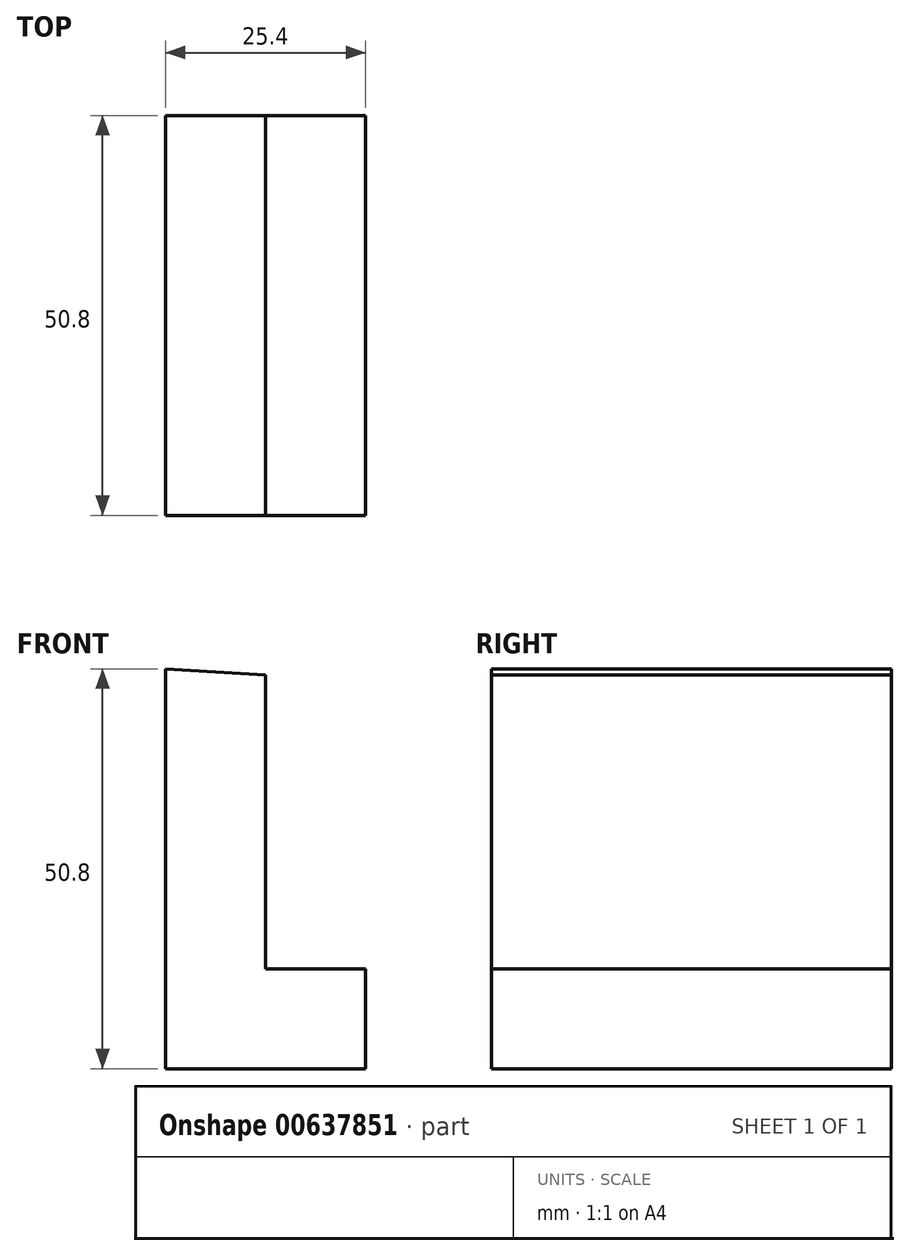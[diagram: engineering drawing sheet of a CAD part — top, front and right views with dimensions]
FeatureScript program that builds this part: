
annotation { "Feature Type Name" : "Feature", "Feature Type Description" : "" }
export const myFeature = defineFeature(function(context is Context, id is Id, definition is map)
    precondition{}
    {
        {
            var Q0;
            Q0=qCreatedBy(makeId("Front.planeOp"),FACE);
            var sketch = newSketch(context, id + "F0", { "sketchPlane" : qUnion([Q0])});
            skLineSegment(sketch, "E0", {"start": v(-66.99, 64.41) * mm, "end": v(-66.99, 13.61) * mm});
            skLineSegment(sketch, "E1", {"start": v(-66.99, 13.61) * mm, "end": v(-41.59, 13.61) * mm});
            skLineSegment(sketch, "E2", {"start": v(-41.59, 13.61) * mm, "end": v(-41.59, 26.31) * mm});
            skLineSegment(sketch, "E3", {"start": v(-41.59, 26.31) * mm, "end": v(-54.29, 26.31) * mm});
            skLineSegment(sketch, "E4", {"start": v(-54.29, 26.31) * mm, "end": v(-54.29, 77.11) * mm});
            skLineSegment(sketch, "E5", {"start": v(-54.29, 77.11) * mm, "end": v(-54.29, 63.61) * mm});
            skLineSegment(sketch, "E6", {"start": v(-54.29, 63.61) * mm, "end": v(-66.99, 64.41) * mm});
            skSolve(sketch);
        }
        {
            var Q0;
            Q0 = qSketchRegion(id + "F0", true);
            extrude(context, id + "F1", {"entities" : qUnion([Q0]), "depth" : 50.8 * mm, "offsetDistance" : 25.4 * mm});
        }
    });
